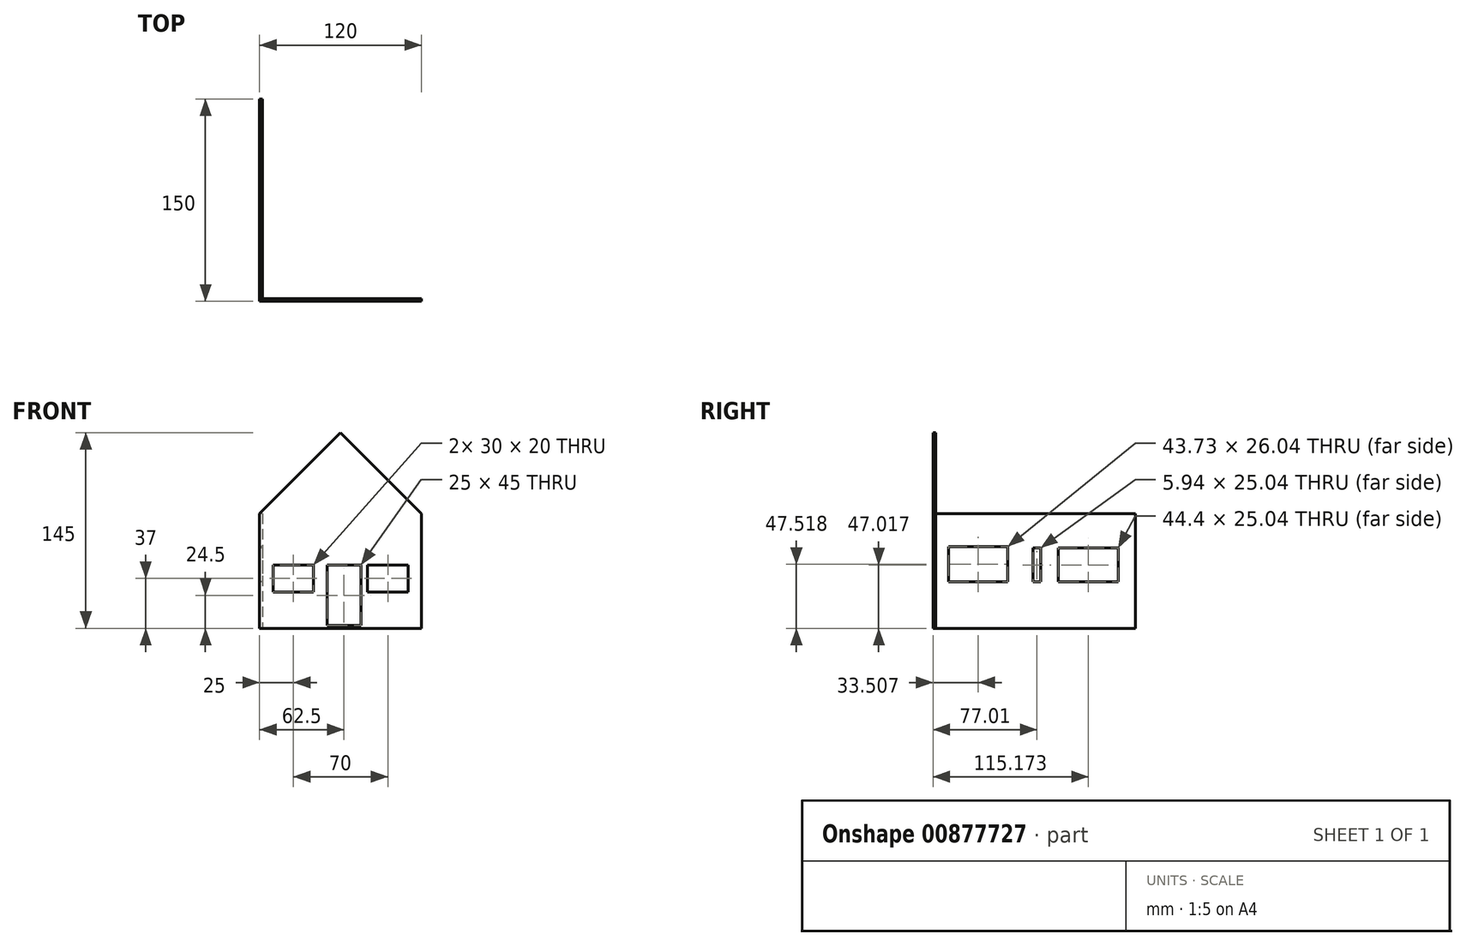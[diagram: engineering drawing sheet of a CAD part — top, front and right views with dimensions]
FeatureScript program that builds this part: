
annotation { "Feature Type Name" : "Feature", "Feature Type Description" : "" }
export const myFeature = defineFeature(function(context is Context, id is Id, definition is map)
    precondition{}
    {
        {
            var Q0;
            Q0=qCreatedBy(makeId("Top.planeOp"),FACE);
            var sketch = newSketch(context, id + "F0", { "sketchPlane" : qUnion([Q0])});
            skLineSegment(sketch, "E0.bottom", {"start": v(-120, 0) * mm, "end": v(0, 0) * mm});
            skLineSegment(sketch, "E0.top", {"start": v(-120, 150) * mm, "end": v(0, 150) * mm});
            skLineSegment(sketch, "E0.left", {"start": v(-120, 0) * mm, "end": v(-120, 150) * mm});
            skLineSegment(sketch, "E0.right", {"start": v(0, 0) * mm, "end": v(0, 150) * mm});
            skLineSegment(sketch, "E1", {"start": v(-120, 2) * mm, "end": v(0, 2) * mm});
            skLineSegment(sketch, "E2", {"start": v(-120, 148) * mm, "end": v(0, 148) * mm});
            skLineSegment(sketch, "E3", {"start": v(-118, 148) * mm, "end": v(-118, 2) * mm});
            skLineSegment(sketch, "E4", {"start": v(-2, 148) * mm, "end": v(-2, 2) * mm});
            skSolve(sketch);
        }
        {
            var Q0;
            Q0=qCreatedBy(makeId("Front.planeOp"),FACE);
            var sketch = newSketch(context, id + "F1", { "sketchPlane" : qUnion([Q0])});
            skLineSegment(sketch, "E5", {"start": v(-120, 0) * mm, "end": v(0, 0) * mm});
            skLineSegment(sketch, "E6", {"start": v(0, 0) * mm, "end": v(0, 85) * mm});
            skLineSegment(sketch, "E7", {"start": v(0, 85) * mm, "end": v(-60, 145) * mm});
            skLineSegment(sketch, "E8", {"start": v(-60, 145) * mm, "end": v(-120, 85) * mm});
            skLineSegment(sketch, "E9", {"start": v(-120, 85) * mm, "end": v(-120, 0) * mm});
            skLineSegment(sketch, "E10.bottom", {"start": v(-110, 47) * mm, "end": v(-80, 47) * mm});
            skLineSegment(sketch, "E10.top", {"start": v(-110, 27) * mm, "end": v(-80, 27) * mm});
            skLineSegment(sketch, "E10.left", {"start": v(-110, 47) * mm, "end": v(-110, 27) * mm});
            skLineSegment(sketch, "E10.right", {"start": v(-80, 47) * mm, "end": v(-80, 27) * mm});
            skLineSegment(sketch, "E11.bottom", {"start": v(-70, 47) * mm, "end": v(-45, 47) * mm});
            skLineSegment(sketch, "E11.top", {"start": v(-70, 2) * mm, "end": v(-45, 2) * mm});
            skLineSegment(sketch, "E11.left", {"start": v(-70, 47) * mm, "end": v(-70, 2) * mm});
            skLineSegment(sketch, "E11.right", {"start": v(-45, 47) * mm, "end": v(-45, 2) * mm});
            skLineSegment(sketch, "E12.bottom", {"start": v(-40, 47) * mm, "end": v(-10, 47) * mm});
            skLineSegment(sketch, "E12.top", {"start": v(-40, 27) * mm, "end": v(-10, 27) * mm});
            skLineSegment(sketch, "E12.left", {"start": v(-40, 47) * mm, "end": v(-40, 27) * mm});
            skLineSegment(sketch, "E12.right", {"start": v(-10, 47) * mm, "end": v(-10, 27) * mm});
            skSolve(sketch);
        }
        {
            var Q0;
            Q0=makeQuery(id+"F1.imprint","IMPRINT",FACE,{"disambiguationData":[TD([[makeQuery(id+"F1.imprint","IMPRINT",EDGE,{"derivedFrom":sQuery(id+"F1.wireOp",EDGE,"E5")}),1.0]])]});
            var Q1;
            Q1=sQuery(id+"F0.wireOp",VERTEX,"E1.end");
            extrude(context, id + "F2", {"entities" : qUnion([Q0]), "endBound" : BoundingType.UP_TO_VERTEX, "oppositeDirection" : true, "depth" : 25 * mm, "endBoundEntityVertex" : qUnion([Q1]), "offsetDistance" : 25 * mm});
        }
        {
            var Q0;
            Q0=qCreatedBy(makeId("Right.planeOp"),FACE);
            var Q1;
            Q1=sQuery(id+"F0.wireOp",VERTEX,"E0.top.start");
            cPlane(context, id + "F3", {"entities" : qUnion([Q0, Q1]), "cplaneType" : CPlaneType.PLANE_POINT, "offset" : 25 * mm, "width" : 150 * mm, "height" : 150 * mm});
        }
        {
            var Q0;
            Q0=qCreatedBy(id+"F3.planeOp",FACE);
            var sketch = newSketch(context, id + "F4", { "sketchPlane" : qUnion([Q0])});
            skLineSegment(sketch, "E13.bottom", {"start": v(137.37, 59.54) * mm, "end": v(92.97, 59.54) * mm});
            skLineSegment(sketch, "E13.top", {"start": v(137.37, 34.5) * mm, "end": v(92.97, 34.5) * mm});
            skLineSegment(sketch, "E13.left", {"start": v(137.37, 59.54) * mm, "end": v(137.37, 34.5) * mm});
            skLineSegment(sketch, "E13.right", {"start": v(92.97, 59.54) * mm, "end": v(92.97, 34.5) * mm});
            skLineSegment(sketch, "E14.bottom", {"start": v(79.98, 59.54) * mm, "end": v(74.04, 59.54) * mm});
            skLineSegment(sketch, "E14.top", {"start": v(79.98, 34.5) * mm, "end": v(74.04, 34.5) * mm});
            skLineSegment(sketch, "E14.left", {"start": v(79.98, 59.54) * mm, "end": v(79.98, 34.5) * mm});
            skLineSegment(sketch, "E14.right", {"start": v(74.04, 59.54) * mm, "end": v(74.04, 34.5) * mm});
            skLineSegment(sketch, "E15.bottom", {"start": v(55.37, 60.54) * mm, "end": v(11.64, 60.54) * mm});
            skLineSegment(sketch, "E15.top", {"start": v(55.37, 34.5) * mm, "end": v(11.64, 34.5) * mm});
            skLineSegment(sketch, "E15.left", {"start": v(55.37, 60.54) * mm, "end": v(55.37, 34.5) * mm});
            skLineSegment(sketch, "E15.right", {"start": v(11.64, 60.54) * mm, "end": v(11.64, 34.5) * mm});
            skLineSegment(sketch, "E16.bottom", {"start": v(150, 85) * mm, "end": v(2, 85) * mm});
            skLineSegment(sketch, "E16.top", {"start": v(150, 0) * mm, "end": v(2, 0) * mm});
            skLineSegment(sketch, "E16.left", {"start": v(150, 85) * mm, "end": v(150, 0) * mm});
            skLineSegment(sketch, "E16.right", {"start": v(2, 85) * mm, "end": v(2, 0) * mm});
            skSolve(sketch);
        }
        {
            var Q0;
            Q0=makeQuery(id+"F4.imprint","IMPRINT",FACE,{"disambiguationData":[TD([[makeQuery(id+"F4.imprint","IMPRINT",EDGE,{"derivedFrom":sQuery(id+"F4.wireOp",EDGE,"E13.bottom")}),-1.0]])]});
            var Q1;
            Q1=sQuery(id+"F0.wireOp",VERTEX,"E3.end");
            extrude(context, id + "F5", {"entities" : qUnion([Q0]), "endBound" : BoundingType.UP_TO_VERTEX, "depth" : 25 * mm, "endBoundEntityVertex" : qUnion([Q1]), "offsetDistance" : 25 * mm});
        }
    });
